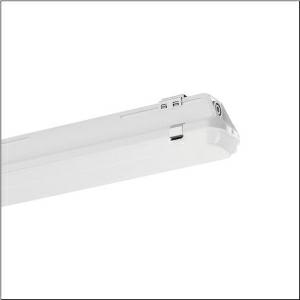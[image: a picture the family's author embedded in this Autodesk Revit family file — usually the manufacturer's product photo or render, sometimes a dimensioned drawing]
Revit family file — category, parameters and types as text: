
# Revit family: monsun_r__11_51fp207p4b0u_9205
name_source: partatom
category: Lighting Fixtures
units: mm (PartAtom-declared; Revit-internal decimal feet)

## family parameters
Cut with Voids When Loaded = No
Host = Face
Light Source = No
Part Type = Normal
Room Calculation Point = No
Round Connector Dimension = Use Diameter
Shared = No

## types (1)
- Monsun® 11 (1 x LED, 10910 lm, 62.4 W, 4000K)
    Apparent Load = 62 VA
    CIE Flux Codes = 45 75 93 94 100
    Color Rendering = 80
    Color Temperature = 4000K
    Default Elevation = 1800 mm
    Description = Monsun® 11, damp-proof luminaire, chain hanger, primary optical cover: enclosure, of PC, light emission: direct distribution, primary light characteristic: symmetric, installation type: suspended mounting, surface-mounted, horizontal mounting, vertical mounting, LED, rated luminous flux: 10.910lm, luminous efficacy: 175lm/W, light colour: 840, colour temperature: 4000K, control gear: ON/OFF, with terminal, 3-pole, max. 2.5mm², mains connection: 220..240V, AC, 50/60Hz, rated input power: 62W, luminaire housing, of glass-fibre reinforced polyester, uncoated, bright grey, incl. chain hanger, length: 1.590mm, width: 90mm, height: 88mm, clip for enclosure, of stainless steel (V2A), ceiling mounting element, of stainless steel (V2A), chain hanger, of stainless steel (V2A), protection rating (complete): IP66, insulation class (complete): insulation class I (protective earthing), certification: CE, ENEC, VDE, UKCA, protection symbol: D, impact resistance: IK08, permissible operating ambient temperature: -35..+35°C, standard: EN 50419, EN 60598-2-1, contact your sales advisor before using the luminaires in applications with unclear chemical exposure, large temperature fluctuations or condensation-forming humidity, LABS conformity tested according to VDMA 24364:2018-05, no direct snow, no direct sun, no direct rain, for indoor or canopied outdoor use, corresponds to IFS (International Featured Standards) requirements for safety and quality in the food industry, packaging unit: 1 piece
    Height = 89 mm
    Lamp = 1 x LED
    Lamp Light Flux = 10910 lm
    Lamp Power = 62.4 W
    Lamp count = 1
    Length = 1590 mm
    Luminous efficacy = 175 lm/W
    Manufacturer = Siteco
    ModVariant = No
    Model = 51FP207P4B0U
    Mounting Place = Ceiling
    Mounting Type = Surface mounted
    Number of Poles = 1
    OnlyDefault = Yes
    Power Factor = 1
    Product Name = Monsun® 11
    Product group = damp-proof luminaire
    ProductGroupID = 300
    Protection Class = Protection class I
    Protection Degree = IP 66
    RLX_Detail_Level = 1
    RLX_Emergency_Light_Flux = 0 lm
    RLX_Emergency_Type = 0
    RLX_Emergency_Type_DB = No
    RlxData = <blob elided: 88313 chars, md5=6d245ccf>
    Socket = socket
    Standby Power = 0 W
    System Light Flux = 10910 lm
    System Power = 62 W
    Type Comments = Product without accessories
    Type Image = l_1349237.jpg
    URL = http://relux.com
    VarID = ---
    Voltage = 0 V
    Weight = 0.00 kg
    Width = 90 mm

## geometry (parser evidence)
native form markers: Blend x4, Sweep x11
no freeform markers — native parametric forms only
